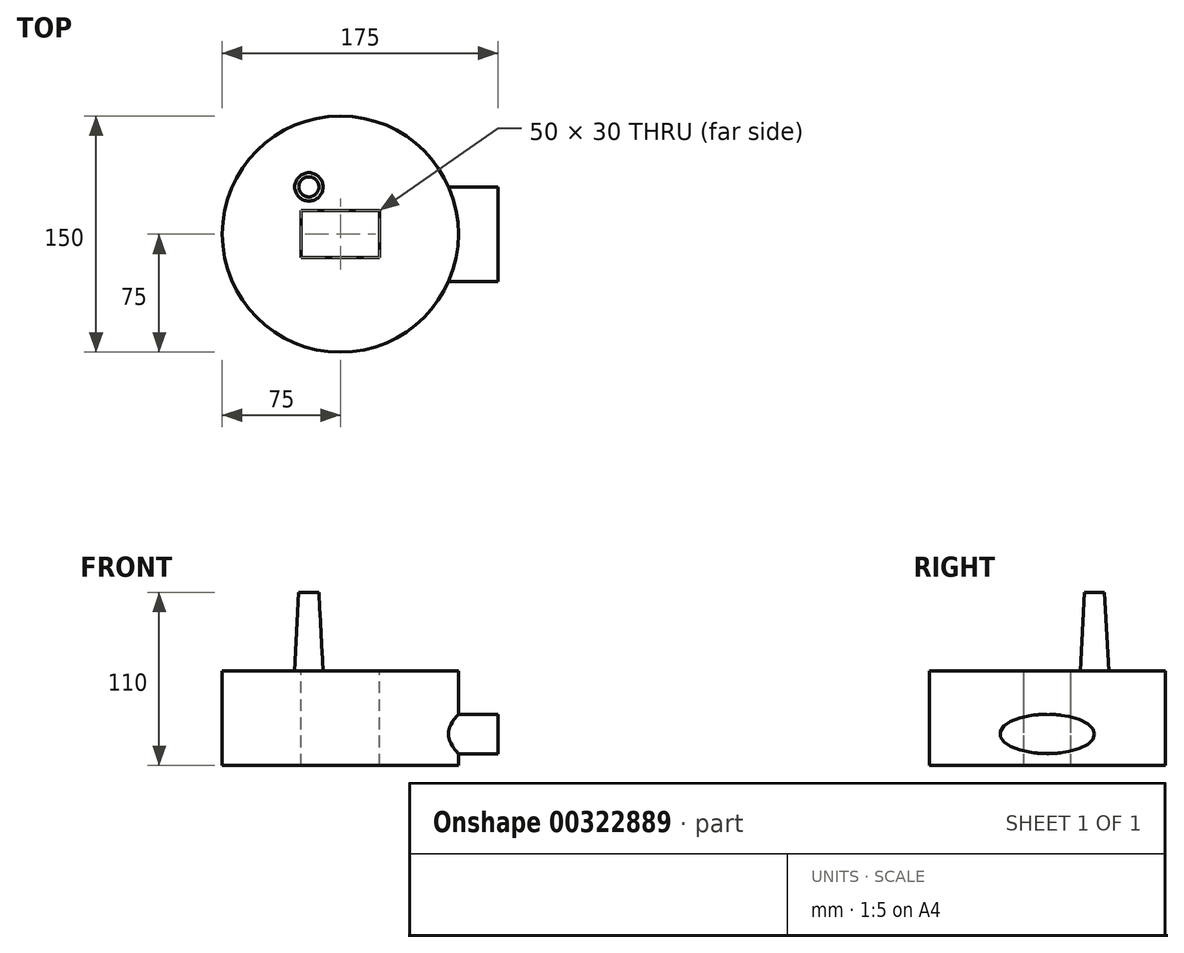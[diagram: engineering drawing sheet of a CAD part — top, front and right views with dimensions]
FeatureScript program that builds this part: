
annotation { "Feature Type Name" : "Feature", "Feature Type Description" : "" }
export const myFeature = defineFeature(function(context is Context, id is Id, definition is map)
    precondition{}
    {
        {
            var Q0;
            Q0=qCreatedBy(makeId("Top.planeOp"),FACE);
            var sketch = newSketch(context, id + "F0", { "sketchPlane" : qUnion([Q0])});
            skCircle(sketch, "E0", {"center": v(0, 0) * mm, "radius": 75 * mm});
            skSolve(sketch);
        }
        {
            var Q0;
            Q0 = qSketchRegion(id + "F0", true);
            extrude(context, id + "F1", {"entities" : qUnion([Q0]), "depth" : 60 * mm});
        }
        {
            var Q0;
            Q0=makeQuery(id+"F1.opExtrude","CAP_FACE",FACE,{"disambiguationData":[OSD([sQuery(id+"F0.wireOp",EDGE,"E0")])],"isStart":false});
            var sketch = newSketch(context, id + "F2", { "sketchPlane" : qUnion([Q0])});
            skLineSegment(sketch, "E1.bottom", {"start": v(25, -15) * mm, "end": v(-25, -15) * mm});
            skLineSegment(sketch, "E1.top", {"start": v(25, 15) * mm, "end": v(-25, 15) * mm});
            skLineSegment(sketch, "E1.left", {"start": v(25, -15) * mm, "end": v(25, 15) * mm});
            skLineSegment(sketch, "E1.right", {"start": v(-25, -15) * mm, "end": v(-25, 15) * mm});
            skPoint(sketch, "E1.middle", {"position": v(0, 0) * mm});
            skSolve(sketch);
        }
        {
            var Q0;
            Q0 = qSketchRegion(id + "F2", true);
            extrude(context, id + "F3", {"entities" : qUnion([Q0]), "operationType" : NewBodyOperationType.REMOVE, "endBound" : BoundingType.THROUGH_ALL, "oppositeDirection" : true, "depth" : 101.32 * mm});
        }
        {
            var Q0;
            Q0=qCreatedBy(makeId("Right.planeOp"),FACE);
            cPlane(context, id + "F4", {"entities" : qUnion([Q0]), "cplaneType" : CPlaneType.OFFSET, "offset" : 100 * mm, "width" : 150 * mm, "height" : 150 * mm});
        }
        {
            var Q0;
            Q0=qCreatedBy(id+"F4.planeOp",FACE);
            var sketch = newSketch(context, id + "F5", { "sketchPlane" : qUnion([Q0])});
            skEllipse(sketch, "E2", {"center": v(0, 20) * mm, "majorRadius": 30 * mm, "minorRadius": 12.5 * mm, "majorAxis": v(1, 0)});
            skSolve(sketch);
        }
        {
            var Q0;
            Q0 = qSketchRegion(id + "F5", true);
            extrude(context, id + "F6", {"entities" : qUnion([Q0]), "operationType" : NewBodyOperationType.ADD, "endBound" : BoundingType.UP_TO_NEXT, "oppositeDirection" : true, "depth" : 32.6 * mm});
        }
        {
            var Q0;
            Q0=makeQuery(id+"F1.opExtrude","CAP_FACE",FACE,{"disambiguationData":[OSD([sQuery(id+"F0.wireOp",EDGE,"E0")])],"isStart":false});
            var sketch = newSketch(context, id + "F7", { "sketchPlane" : qUnion([Q0])});
            skCircle(sketch, "E3", {"center": v(-20, 30) * mm, "radius": 9 * mm});
            skSolve(sketch);
        }
        {
            var Q0;
            Q0 = qSketchRegion(id + "F7", true);
            extrude(context, id + "F8", {"entities" : qUnion([Q0]), "operationType" : NewBodyOperationType.ADD, "depth" : 50 * mm, "hasDraft" : true, "draftAngle" : 3 * degree, "draftPullDirection" : true});
        }
    });
